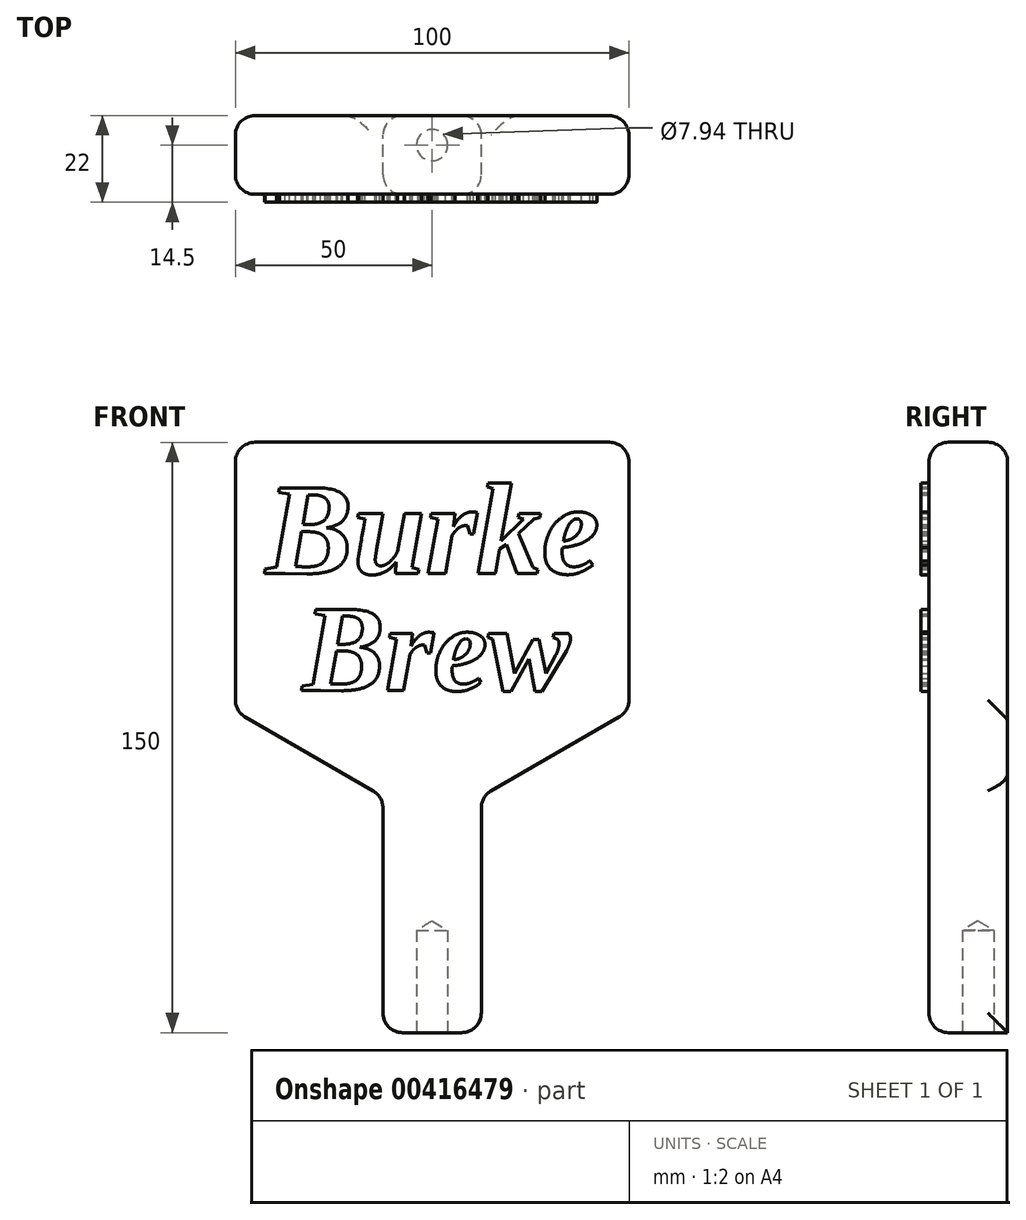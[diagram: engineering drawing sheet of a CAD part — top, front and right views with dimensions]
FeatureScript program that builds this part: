
annotation { "Feature Type Name" : "Feature", "Feature Type Description" : "" }
export const myFeature = defineFeature(function(context is Context, id is Id, definition is map)
    precondition{}
    {
        {
            var Q0;
            Q0=qCreatedBy(makeId("Front.planeOp"),FACE);
            var sketch = newSketch(context, id + "F0", { "sketchPlane" : qUnion([Q0])});
            skLineSegment(sketch, "E0", {"start": v(0, 61.21) * mm, "end": v(50, 61.21) * mm});
            skLineSegment(sketch, "E1", {"start": v(50, 61.21) * mm, "end": v(50, -7.14) * mm});
            skLineSegment(sketch, "E2", {"start": v(50, -7.14) * mm, "end": v(12.5, -28.79) * mm});
            skLineSegment(sketch, "E3", {"start": v(12.5, -28.79) * mm, "end": v(12.5, -88.79) * mm});
            skLineSegment(sketch, "E4", {"start": v(12.5, -88.79) * mm, "end": v(0, -88.79) * mm});
            skLineSegment(sketch, "E5", {"start": v(0, 61.21) * mm, "end": v(0, -88.79) * mm, "construction": true});
            skLineSegment(sketch, "E6.MirrorCS", {"start": v(0, 61.21) * mm, "end": v(-50, 61.21) * mm});
            skLineSegment(sketch, "E7.MirrorCS", {"start": v(-50, 61.21) * mm, "end": v(-50, -7.14) * mm});
            skLineSegment(sketch, "E8.MirrorCS", {"start": v(-50, -7.14) * mm, "end": v(-12.5, -28.79) * mm});
            skLineSegment(sketch, "E9.MirrorCS", {"start": v(-12.5, -28.79) * mm, "end": v(-12.5, -88.79) * mm});
            skLineSegment(sketch, "E10.MirrorCS", {"start": v(-12.5, -88.79) * mm, "end": v(0, -88.79) * mm});
            skSolve(sketch);
        }
        {
            var Q0;
            Q0 = qSketchRegion(id + "F0", true);
            extrude(context, id + "F1", {"entities" : qUnion([Q0]), "depth" : 20 * mm});
        }
        {
            var Q0;
            Q0=makeQuery(id+"F1.opExtrude","SWEPT_FACE",FACE,{"disambiguationData":[OSD([sQuery(id+"F0.wireOp",EDGE,"E1")])]});
            var Q1;
            Q1=makeQuery(id+"F1.opExtrude","CAP_FACE",FACE,{"disambiguationData":[OSD([sQuery(id+"F0.wireOp",EDGE,"E0"),sQuery(id+"F0.wireOp",EDGE,"E1"),sQuery(id+"F0.wireOp",EDGE,"E2"),sQuery(id+"F0.wireOp",EDGE,"E3"),sQuery(id+"F0.wireOp",EDGE,"E4"),sQuery(id+"F0.wireOp",EDGE,"E6.MirrorCS"),sQuery(id+"F0.wireOp",EDGE,"E7.MirrorCS"),sQuery(id+"F0.wireOp",EDGE,"E8.MirrorCS"),sQuery(id+"F0.wireOp",EDGE,"E9.MirrorCS"),sQuery(id+"F0.wireOp",EDGE,"E10.MirrorCS")])],"isStart":false});
            var Q2;
            Q2=makeQuery(id+"F1.opExtrude","SWEPT_FACE",FACE,{"disambiguationData":[OSD([sQuery(id+"F0.wireOp",EDGE,"E0"),sQuery(id+"F0.wireOp",EDGE,"E6.MirrorCS")])]});
            var Q3;
            Q3=makeQuery(id+"F1.opExtrude","SWEPT_FACE",FACE,{"disambiguationData":[OSD([sQuery(id+"F0.wireOp",EDGE,"E3")])]});
            var Q4;
            Q4=makeQuery(id+"F1.opExtrude","SWEPT_FACE",FACE,{"disambiguationData":[OSD([sQuery(id+"F0.wireOp",EDGE,"E9.MirrorCS")])]});
            var Q5;
            Q5=makeQuery(id+"F1.opExtrude","SWEPT_FACE",FACE,{"disambiguationData":[OSD([sQuery(id+"F0.wireOp",EDGE,"E7.MirrorCS")])]});
            fillet(context, id + "F2", {"entities" : qUnion([Q0, Q1, Q2, Q3, Q4, Q5]), "radius" : 5 * mm, "tangentPropagation" : true, "allowEdgeOverflow" : false});
        }
        {
            var Q0;
            Q0=makeQuery(id+"F1.opExtrude","SWEPT_FACE",FACE,{"disambiguationData":[OSD([sQuery(id+"F0.wireOp",EDGE,"E4"),sQuery(id+"F0.wireOp",EDGE,"E10.MirrorCS")])]});
            var sketch = newSketch(context, id + "F3", { "sketchPlane" : qUnion([Q0])});
            skLineSegment(sketch, "E11", {"start": v(7.5, 15) * mm, "end": v(-7.5, 0) * mm, "construction": true});
            skPoint(sketch, "E12", {"position": v(0, 7.5) * mm});
            skSolve(sketch);
        }
        {
            var Q0;
            Q0=sQuery(id+"F3.wireOp",VERTEX,"E12");
            var Q1;
            Q1=makeQuery(id+"F1.opExtrude","SWEPT_BODY",BODY,{"disambiguationData":[OSD([sQuery(id+"F0.wireOp",EDGE,"E0"),sQuery(id+"F0.wireOp",EDGE,"E1"),sQuery(id+"F0.wireOp",EDGE,"E2"),sQuery(id+"F0.wireOp",EDGE,"E3"),sQuery(id+"F0.wireOp",EDGE,"E4"),sQuery(id+"F0.wireOp",EDGE,"E6.MirrorCS"),sQuery(id+"F0.wireOp",EDGE,"E7.MirrorCS"),sQuery(id+"F0.wireOp",EDGE,"E8.MirrorCS"),sQuery(id+"F0.wireOp",EDGE,"E9.MirrorCS"),sQuery(id+"F0.wireOp",EDGE,"E10.MirrorCS")])]});
            hole(context, id + "F4", {"style" : HoleStyle.SIMPLE, "endStyle" : HoleEndStyle.BLIND, "standardTappedOrClearance" : lookupTablePath({ "standard" : "ANSI", "engagement" : "75%", "pitch" : "16 tpi", "size" : "3/8", "type" : "Tapped" }), "standardBlindInLast" : lookupTablePath({ "standard" : "ANSI", "engagement" : "75%", "pitch" : "16 tpi", "size" : "3/8", "type" : "Tapped" }), "holeDiameter" : 7.94 * mm, "showTappedDepth" : true, "holeDepth" : 26 * mm, "isTappedThrough" : true, "tappedDepth" : 19.65 * mm, "tapClearance" : 4, "startFromSketch" : true, "locations" : qUnion([Q0]), "scope" : qUnion([Q1]), "majorDiameter" : 9.53 * mm});
        }
        {
            var Q0;
            Q0=makeQuery(id+"F1.opExtrude","CAP_FACE",FACE,{"disambiguationData":[OSD([sQuery(id+"F0.wireOp",EDGE,"E0"),sQuery(id+"F0.wireOp",EDGE,"E1"),sQuery(id+"F0.wireOp",EDGE,"E2"),sQuery(id+"F0.wireOp",EDGE,"E3"),sQuery(id+"F0.wireOp",EDGE,"E4"),sQuery(id+"F0.wireOp",EDGE,"E6.MirrorCS"),sQuery(id+"F0.wireOp",EDGE,"E7.MirrorCS"),sQuery(id+"F0.wireOp",EDGE,"E8.MirrorCS"),sQuery(id+"F0.wireOp",EDGE,"E9.MirrorCS"),sQuery(id+"F0.wireOp",EDGE,"E10.MirrorCS")])],"isStart":false});
            var sketch = newSketch(context, id + "F5", { "sketchPlane" : qUnion([Q0])});
            skText(sketch, "E13", { "text": "Burke", "fontName": "Tinos-BoldItalic.ttf"});
            const initialGuessF5  = {"E13": [-0.04227, 0.02788, 1, 0, 0.0239]};
            skSetInitialGuess(sketch, initialGuessF5);
            skSolve(sketch);
        }
        {
            var Q0;
            Q0 = qSketchRegion(id + "F5", true);
            extrude(context, id + "F6", {"entities" : qUnion([Q0]), "operationType" : NewBodyOperationType.ADD, "depth" : 2 * mm});
        }
        {
            var Q0;
            {var subQ0=sQuery(id+"F0.wireOp",EDGE,"E8.MirrorCS");var subQ1=sQuery(id+"F0.wireOp",EDGE,"E7.MirrorCS");var subQ2=sQuery(id+"F0.wireOp",EDGE,"E10.MirrorCS");var subQ3=sQuery(id+"F0.wireOp",EDGE,"E4");var subQ4=sQuery(id+"F0.wireOp",EDGE,"E2");var subQ5=sQuery(id+"F0.wireOp",EDGE,"E1");var subQ6=sQuery(id+"F0.wireOp",EDGE,"E3");var subQ7=sQuery(id+"F0.wireOp",EDGE,"E0");var subQ8=sQuery(id+"F0.wireOp",EDGE,"E9.MirrorCS");var subQ9=sQuery(id+"F0.wireOp",EDGE,"E6.MirrorCS");Q0=makeQuery(id+"F6.boolean.opBoolean","SPLIT",FACE,{"disambiguationData":[TD([makeQuery(id+"F6.opExtrude","SWEPT_FACE",FACE,{"disambiguationData":[OSD([sQuery(id+"F5.wireOp",EDGE,"E13.sketch_text.stroke-13")])]})])],"derivedFrom":makeQuery(id+"F1.opExtrude","CAP_FACE",FACE,{"disambiguationData":[OSD([subQ7,subQ5,subQ4,subQ6,subQ3,subQ9,subQ1,subQ0,subQ8,subQ2])],"isStart":false})});}
            var sketch = newSketch(context, id + "F7", { "sketchPlane" : qUnion([Q0])});
            skText(sketch, "E14", { "text": "Brew", "fontName": "Tinos-BoldItalic.ttf"});
            const initialGuessF7  = {"E14": [-0.03293, -0.00182, 1, 0, 0.02258]};
            skSetInitialGuess(sketch, initialGuessF7);
            skSolve(sketch);
        }
        {
            var Q0;
            Q0 = qSketchRegion(id + "F7", true);
            extrude(context, id + "F8", {"entities" : qUnion([Q0]), "operationType" : NewBodyOperationType.ADD, "depth" : 2 * mm});
        }
    });
